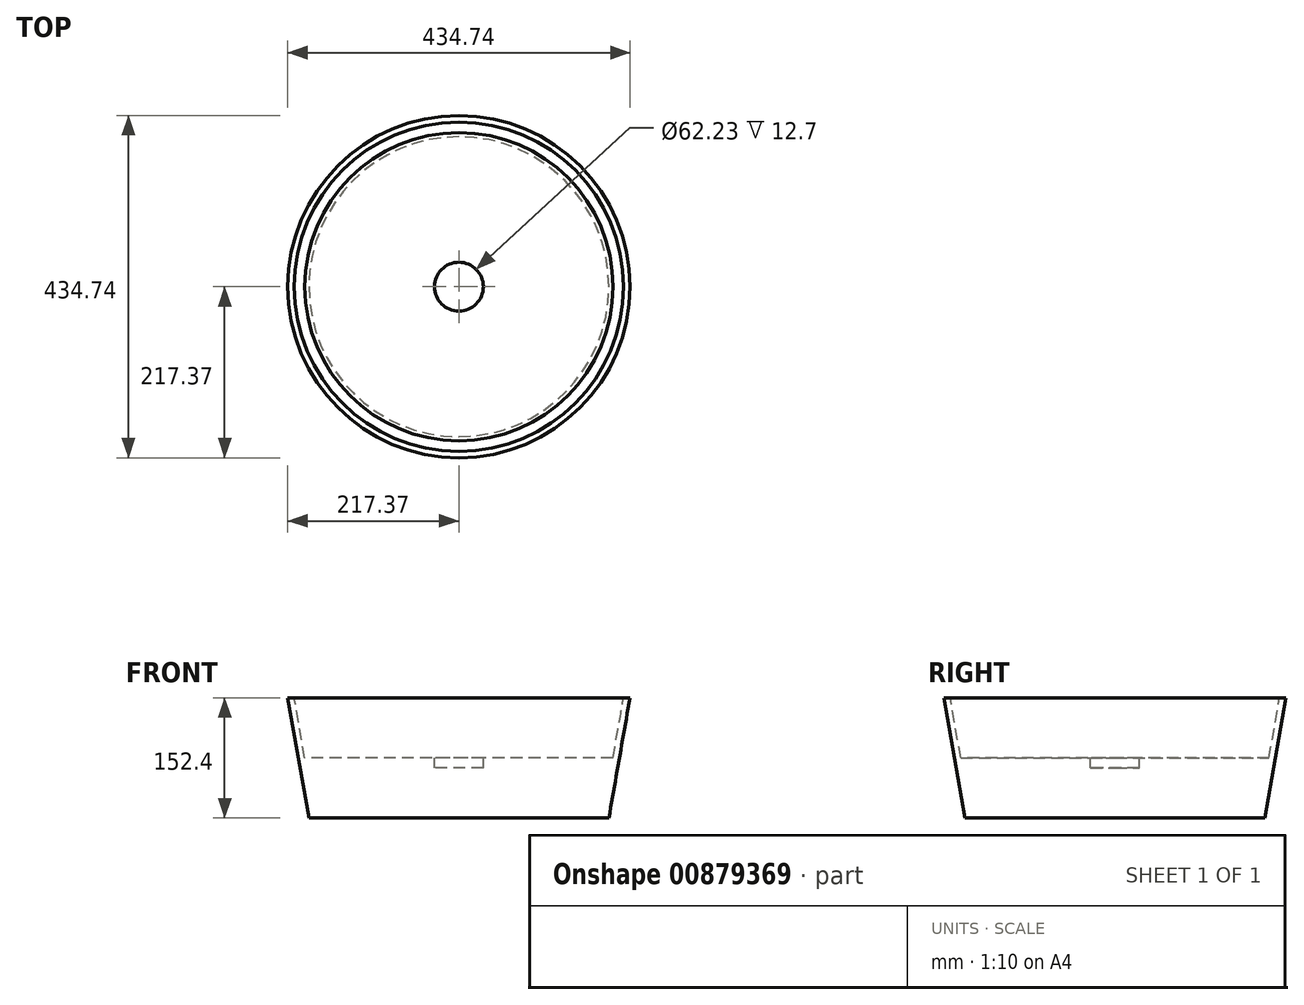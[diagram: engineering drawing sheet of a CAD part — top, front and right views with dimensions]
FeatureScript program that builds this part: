
annotation { "Feature Type Name" : "Feature", "Feature Type Description" : "" }
export const myFeature = defineFeature(function(context is Context, id is Id, definition is map)
    precondition{}
    {
        {
            var Q0;
            Q0=qCreatedBy(makeId("Top.planeOp"),FACE);
            var sketch = newSketch(context, id + "F0", { "sketchPlane" : qUnion([Q0])});
            skCircle(sketch, "E0", {"center": v(0, 0) * mm, "radius": 190.5 * mm});
            skSolve(sketch);
        }
        {
            var Q0;
            Q0 = qSketchRegion(id + "F0", true);
            extrude(context, id + "F1", {"entities" : qUnion([Q0]), "depth" : 152.4 * mm, "offsetDistance" : 25.4 * mm, "hasDraft" : true, "draftAngle" : 10 * degree});
        }
        {
            var Q0;
            Q0=makeQuery(id+"F1.opExtrude","CAP_FACE",FACE,{"disambiguationData":[OSD([sQuery(id+"F0.wireOp",EDGE,"E0")])],"isStart":false});
            var sketch = newSketch(context, id + "F2", { "sketchPlane" : qUnion([Q0])});
            skCircle(sketch, "E1", {"center": v(0, 0) * mm, "radius": 31.12 * mm});
            skSolve(sketch);
        }
        {
            var Q0;
            Q0 = qSketchRegion(id + "F2", true);
            extrude(context, id + "F3", {"entities" : qUnion([Q0]), "operationType" : NewBodyOperationType.REMOVE, "oppositeDirection" : true, "depth" : 88.9 * mm, "offsetDistance" : 25.4 * mm});
        }
        {
            var Q0;
            Q0=makeQuery(id+"F1.opExtrude","CAP_FACE",FACE,{"disambiguationData":[OSD([sQuery(id+"F0.wireOp",EDGE,"E0")])],"isStart":false});
            var sketch = newSketch(context, id + "F4", { "sketchPlane" : qUnion([Q0])});
            skCircle(sketch, "E2", {"center": v(0, 0) * mm, "radius": 209.15 * mm});
            skSolve(sketch);
        }
        {
            var Q0;
            Q0 = qSketchRegion(id + "F4", true);
            extrude(context, id + "F5", {"entities" : qUnion([Q0]), "operationType" : NewBodyOperationType.REMOVE, "oppositeDirection" : true, "depth" : 76.2 * mm, "offsetDistance" : 25.4 * mm, "hasDraft" : true, "draftAngle" : 10 * degree, "draftPullDirection" : true});
        }
    });
